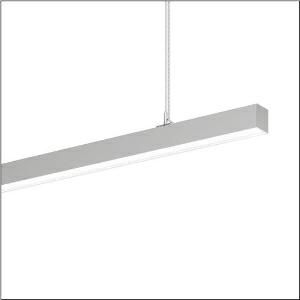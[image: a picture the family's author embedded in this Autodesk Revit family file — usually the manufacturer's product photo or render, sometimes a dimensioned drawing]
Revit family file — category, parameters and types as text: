
# Revit family: silica_r__21_51mx30tct9s_9c67
name_source: partatom
category: Lighting Fixtures
units: mm (PartAtom-declared; Revit-internal decimal feet)

## family parameters
Cut with Voids When Loaded = No
Host = Face
Light Source = No
Part Type = Normal
Room Calculation Point = No
Round Connector Dimension = Use Diameter
Shared = No

## types (1)
- --- (1 x LED, 10300 lm, 84.4 W, 6500K)
    Apparent Load = 84 VA
    CIE Flux Codes = 47 79 96 58 100
    Color Rendering = 80
    Color Temperature = 6500K
    Default Elevation = 1800 mm
    Description = Silica® 21, office luminaire, primary optical cover: cover, of PMMA, opal, light emission: direct/indirect distribution, primary light characteristic: symmetric, installation type: suspended mounting, LED, rated luminous flux: 10.300lm, luminous efficacy: 116lm/W, light colour: 8tw, colour temperature: 2700..6500K, control gear: ECG DALI, with terminal, 3+2-pole, max. 2.5mm², mains connection: 220..240V, AC, 50/60Hz, rated input power: 88.7W, luminaire housing, of aluminium, metallic grey (RAL 9006), length: 3.004mm, width: 53mm, height: 53mm, protection rating (complete): IP20, insulation class (complete): insulation class I (protective earthing), certification: CE, permissible operating ambient temperature: 0..+35°C, standard: EN 50419, packaging unit: 1 piece
    Height = 53 mm
    Lamp = 1 x LED
    Lamp Light Flux = 10300 lm
    Lamp Power = 84.4 W
    Lamp count = 1
    Length = 3004 mm
    Luminous efficacy = 122 lm/W
    Manufacturer = Siteco
    ModVariant = No
    Model = 51MX30TCT9S
    Mounting Place = Ceiling
    Mounting Type = Pendant
    Number of Poles = 1
    OnlyDefault = Yes
    Power Factor = 1
    Product Name = Silica® 21
    Product group = office luminaire | ceiling pendant
    ProductGroupID = 902
    Protection Class = Protection class I
    Protection Degree = IP 20
    RLX_Detail_Level = 1
    RLX_Emergency_Light_Flux = 0 lm
    RLX_Emergency_Type = 0
    RLX_Emergency_Type_DB = No
    RlxData = <blob elided: 20053 chars, md5=21f8d420>
    Socket = socket
    Standby Power = 0 W
    System Light Flux = 10300 lm
    System Power = 84 W
    Type Comments = individual setting
    Type Image = l_1297747.jpg
    URL = http://relux.com
    VarID = @adj_070933
    Voltage = 0 V
    Weight = 0.00 kg
    Width = 53 mm

## geometry (parser evidence)
native form markers: Blend x4, Sweep x11
no freeform markers — native parametric forms only
